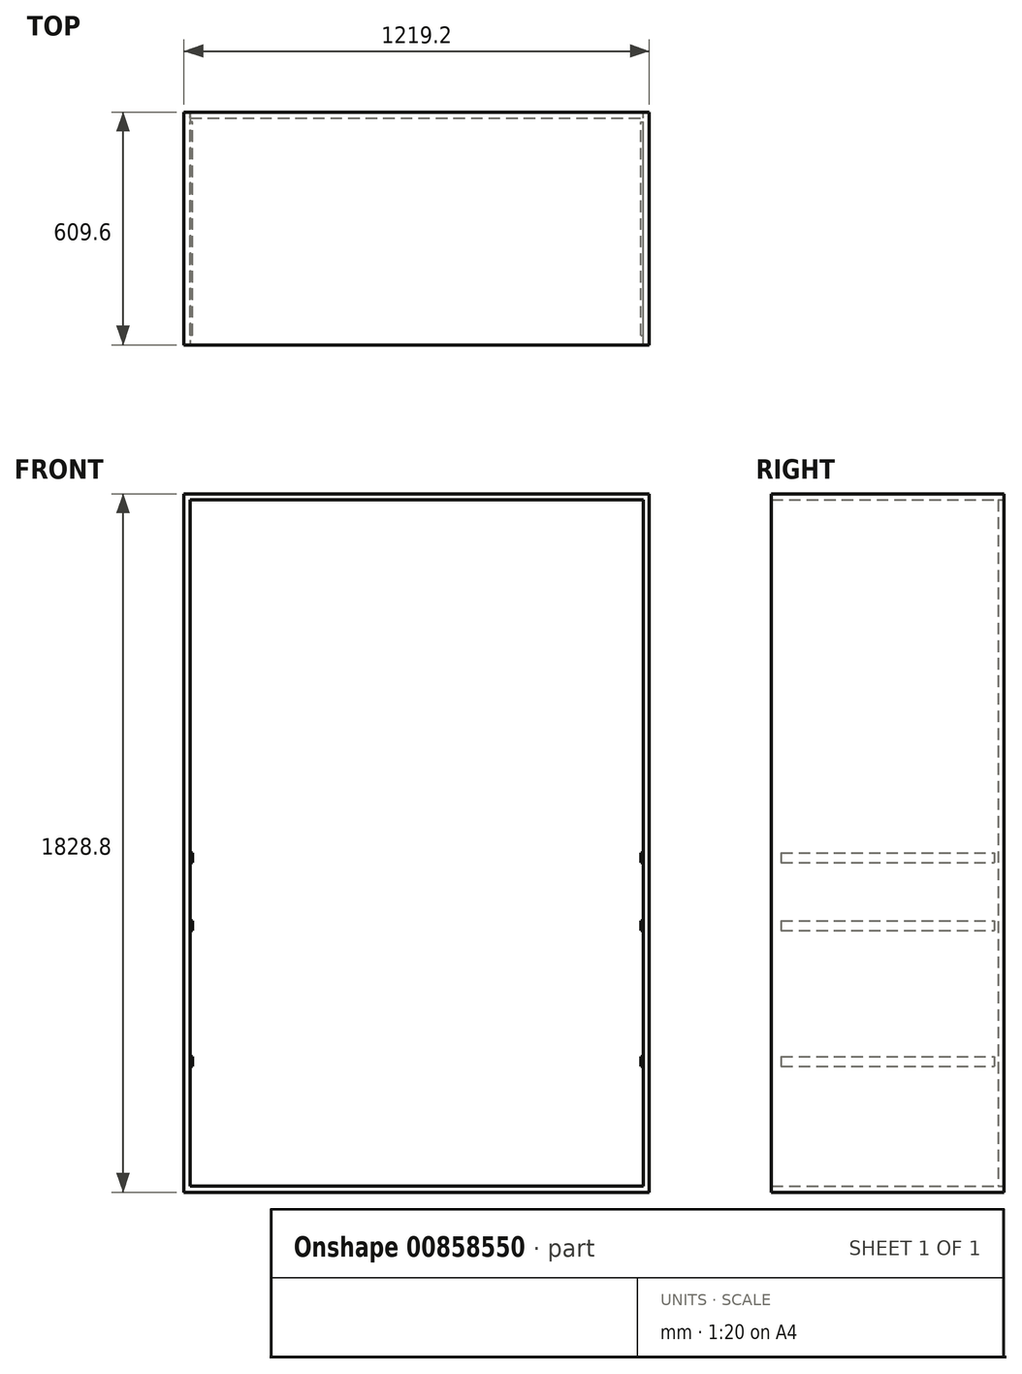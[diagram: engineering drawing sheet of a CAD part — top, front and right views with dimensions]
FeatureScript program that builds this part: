
annotation { "Feature Type Name" : "Feature", "Feature Type Description" : "" }
export const myFeature = defineFeature(function(context is Context, id is Id, definition is map)
    precondition{}
    {
        {
            var Q0;
            Q0=qCreatedBy(makeId("Top.planeOp"),FACE);
            var sketch = newSketch(context, id + "F0", { "sketchPlane" : qUnion([Q0])});
            skLineSegment(sketch, "E0.bottom", {"start": v(-609.6, 304.8) * mm, "end": v(609.6, 304.8) * mm});
            skLineSegment(sketch, "E0.top", {"start": v(-609.6, -304.8) * mm, "end": v(609.6, -304.8) * mm});
            skLineSegment(sketch, "E0.left", {"start": v(-609.6, 304.8) * mm, "end": v(-609.6, -304.8) * mm});
            skLineSegment(sketch, "E0.right", {"start": v(609.6, 304.8) * mm, "end": v(609.6, -304.8) * mm});
            skSolve(sketch);
        }
        {
            var Q0;
            Q0=makeQuery(id+"F0.imprint","IMPRINT",FACE,{"disambiguationData":[TD([[makeQuery(id+"F0.imprint","IMPRINT",EDGE,{"derivedFrom":sQuery(id+"F0.wireOp",EDGE,"E0.bottom")}),-1.0]])]});
            extrude(context, id + "F1", {"entities" : qUnion([Q0]), "depth" : 15.88 * mm, "offsetDistance" : 25.4 * mm});
        }
        {
            var Q0;
            Q0=makeQuery(id+"F1.opExtrude","SWEPT_FACE",FACE,{"disambiguationData":[OSD([sQuery(id+"F0.wireOp",EDGE,"E0.left")])]});
            var sketch = newSketch(context, id + "F2", { "sketchPlane" : qUnion([Q0])});
            skLineSegment(sketch, "E1.bottom", {"start": v(304.8, 0) * mm, "end": v(-304.8, 0) * mm});
            skLineSegment(sketch, "E1.top", {"start": v(304.8, 1828.8) * mm, "end": v(-304.8, 1828.8) * mm});
            skLineSegment(sketch, "E1.left", {"start": v(304.8, 0) * mm, "end": v(304.8, 1828.8) * mm});
            skLineSegment(sketch, "E1.right", {"start": v(-304.8, 0) * mm, "end": v(-304.8, 1828.8) * mm});
            skSolve(sketch);
        }
        {
            var Q0;
            Q0 = qSketchRegion(id + "F2", true);
            extrude(context, id + "F3", {"entities" : qUnion([Q0]), "operationType" : NewBodyOperationType.ADD, "oppositeDirection" : true, "depth" : 15.88 * mm, "offsetDistance" : 25.4 * mm});
        }
        {
            var Q0;
            Q0=makeQuery(id+"F3.opExtrude","SWEPT_FACE",FACE,{"disambiguationData":[OSD([sQuery(id+"F2.wireOp",EDGE,"E1.top")])]});
            var sketch = newSketch(context, id + "F4", { "sketchPlane" : qUnion([Q0])});
            skLineSegment(sketch, "E2.bottom", {"start": v(-609.6, 304.8) * mm, "end": v(609.6, 304.8) * mm});
            skLineSegment(sketch, "E2.top", {"start": v(-609.6, -304.8) * mm, "end": v(609.6, -304.8) * mm});
            skLineSegment(sketch, "E2.left", {"start": v(-609.6, 304.8) * mm, "end": v(-609.6, -304.8) * mm});
            skLineSegment(sketch, "E2.right", {"start": v(609.6, 304.8) * mm, "end": v(609.6, -304.8) * mm});
            skSolve(sketch);
        }
        {
            var Q0;
            {var subQ2=sQuery(id+"F4.wireOp",EDGE,"E2.right");Q0=makeQuery(id+"F4.imprint","IMPRINT",FACE,{"disambiguationData":[TD([[makeQuery(id+"F4.imprint","IMPRINT",EDGE,{"derivedFrom":subQ2}),-1.0]])]});}
            extrude(context, id + "F5", {"entities" : qUnion([Q0]), "operationType" : NewBodyOperationType.ADD, "oppositeDirection" : true, "depth" : 15.88 * mm, "offsetDistance" : 25.4 * mm});
        }
        {
            var Q0;
            Q0=makeQuery(id+"F3.opExtrude","CAP_FACE",FACE,{"disambiguationData":[OSD([sQuery(id+"F2.wireOp",EDGE,"E1.bottom"),sQuery(id+"F2.wireOp",EDGE,"E1.top"),sQuery(id+"F2.wireOp",EDGE,"E1.left"),sQuery(id+"F2.wireOp",EDGE,"E1.right")])],"isStart":false});
            var sketch = newSketch(context, id + "F6", { "sketchPlane" : qUnion([Q0])});
            skLineSegment(sketch, "E3.bottom", {"start": v(-279.4, 355.6) * mm, "end": v(279.4, 355.6) * mm});
            skLineSegment(sketch, "E3.top", {"start": v(-279.4, 330.2) * mm, "end": v(279.4, 330.2) * mm});
            skLineSegment(sketch, "E3.left", {"start": v(-279.4, 355.6) * mm, "end": v(-279.4, 330.2) * mm});
            skLineSegment(sketch, "E3.right", {"start": v(279.4, 355.6) * mm, "end": v(279.4, 330.2) * mm});
            skLineSegment(sketch, "E4.bottom", {"start": v(-279.4, 711.2) * mm, "end": v(279.4, 711.2) * mm});
            skLineSegment(sketch, "E4.top", {"start": v(-279.4, 685.8) * mm, "end": v(279.4, 685.8) * mm});
            skLineSegment(sketch, "E4.left", {"start": v(-279.4, 711.2) * mm, "end": v(-279.4, 685.8) * mm});
            skLineSegment(sketch, "E4.right", {"start": v(279.4, 711.2) * mm, "end": v(279.4, 685.8) * mm});
            skLineSegment(sketch, "E5.bottom", {"start": v(-279.4, 889) * mm, "end": v(279.4, 889) * mm});
            skLineSegment(sketch, "E5.top", {"start": v(-279.4, 863.6) * mm, "end": v(279.4, 863.6) * mm});
            skLineSegment(sketch, "E5.left", {"start": v(-279.4, 889) * mm, "end": v(-279.4, 863.6) * mm});
            skLineSegment(sketch, "E5.right", {"start": v(279.4, 889) * mm, "end": v(279.4, 863.6) * mm});
            skSolve(sketch);
        }
        {
            var Q0;
            Q0 = qSketchRegion(id + "F6", true);
            extrude(context, id + "F7", {"entities" : qUnion([Q0]), "operationType" : NewBodyOperationType.ADD, "depth" : 6.35 * mm, "offsetDistance" : 25.4 * mm});
        }
        {
            var Q0;
            Q0=makeQuery(id+"F1.opExtrude","SWEPT_FACE",FACE,{"disambiguationData":[OSD([sQuery(id+"F0.wireOp",EDGE,"E0.right")])]});
            var sketch = newSketch(context, id + "F8", { "sketchPlane" : qUnion([Q0])});
            skLineSegment(sketch, "E6.bottom", {"start": v(-304.8, 0) * mm, "end": v(304.8, 0) * mm});
            skLineSegment(sketch, "E6.top", {"start": v(-304.8, 1828.8) * mm, "end": v(304.8, 1828.8) * mm});
            skLineSegment(sketch, "E6.left", {"start": v(-304.8, 0) * mm, "end": v(-304.8, 1828.8) * mm});
            skLineSegment(sketch, "E6.right", {"start": v(304.8, 0) * mm, "end": v(304.8, 1828.8) * mm});
            skSolve(sketch);
        }
        {
            var Q0;
            Q0 = qSketchRegion(id + "F8", true);
            extrude(context, id + "F9", {"entities" : qUnion([Q0]), "operationType" : NewBodyOperationType.ADD, "oppositeDirection" : true, "depth" : 15.88 * mm, "offsetDistance" : 25.4 * mm});
        }
        {
            var Q0;
            Q0=makeQuery(id+"F9.boolean.opBoolean","MERGE",FACE,{"derivedFrom":[makeQuery(id+"F5.boolean.opBoolean","MERGE",FACE,{"derivedFrom":[makeQuery(id+"F3.boolean.opBoolean","MERGE",FACE,{"derivedFrom":[makeQuery(id+"F1.opExtrude","SWEPT_FACE",FACE,{"disambiguationData":[OSD([sQuery(id+"F0.wireOp",EDGE,"E0.bottom")])]}),makeQuery(id+"F3.opExtrude","SWEPT_FACE",FACE,{"disambiguationData":[OSD([sQuery(id+"F2.wireOp",EDGE,"E1.right")])]})]}),makeQuery(id+"F5.opExtrude","SWEPT_FACE",FACE,{"disambiguationData":[OSD([sQuery(id+"F4.wireOp",EDGE,"E2.bottom")])]})]}),makeQuery(id+"F9.opExtrude","SWEPT_FACE",FACE,{"disambiguationData":[OSD([sQuery(id+"F8.wireOp",EDGE,"E6.right")])]})]});
            var sketch = newSketch(context, id + "F10", { "sketchPlane" : qUnion([Q0])});
            skLineSegment(sketch, "E7.bottom", {"start": v(-609.6, 0) * mm, "end": v(609.6, 0) * mm});
            skLineSegment(sketch, "E7.top", {"start": v(-609.6, 1828.8) * mm, "end": v(609.6, 1828.8) * mm});
            skLineSegment(sketch, "E7.left", {"start": v(-609.6, 0) * mm, "end": v(-609.6, 1828.8) * mm});
            skLineSegment(sketch, "E7.right", {"start": v(609.6, 0) * mm, "end": v(609.6, 1828.8) * mm});
            skSolve(sketch);
        }
        {
            var Q0;
            Q0=makeQuery(id+"F10.imprint","IMPRINT",FACE,{"disambiguationData":[TD([[makeQuery(id+"F10.imprint","IMPRINT",EDGE,{"derivedFrom":makeQuery(id+"F3.opExtrude","CAP_EDGE",EDGE,{"disambiguationData":[OSD([sQuery(id+"F2.wireOp",EDGE,"E1.right")])],"isStart":false})}),-1.0]])]});
            extrude(context, id + "F11", {"entities" : qUnion([Q0]), "oppositeDirection" : true, "depth" : 15.88 * mm, "offsetDistance" : 25.4 * mm});
        }
        {
            var Q0;
            Q0=makeQuery(id+"F9.opExtrude","CAP_FACE",FACE,{"disambiguationData":[OSD([sQuery(id+"F8.wireOp",EDGE,"E6.bottom"),sQuery(id+"F8.wireOp",EDGE,"E6.top"),sQuery(id+"F8.wireOp",EDGE,"E6.left"),sQuery(id+"F8.wireOp",EDGE,"E6.right")])],"isStart":false});
            var sketch = newSketch(context, id + "F12", { "sketchPlane" : qUnion([Q0])});
            skLineSegment(sketch, "E8.bottom", {"start": v(279.4, 330.2) * mm, "end": v(-279.4, 330.2) * mm});
            skLineSegment(sketch, "E8.top", {"start": v(279.4, 355.6) * mm, "end": v(-279.4, 355.6) * mm});
            skLineSegment(sketch, "E8.left", {"start": v(279.4, 330.2) * mm, "end": v(279.4, 355.6) * mm});
            skLineSegment(sketch, "E8.right", {"start": v(-279.4, 330.2) * mm, "end": v(-279.4, 355.6) * mm});
            skLineSegment(sketch, "E9.bottom", {"start": v(279.4, 685.8) * mm, "end": v(-279.4, 685.8) * mm});
            skLineSegment(sketch, "E9.top", {"start": v(279.4, 711.2) * mm, "end": v(-279.4, 711.2) * mm});
            skLineSegment(sketch, "E9.left", {"start": v(279.4, 685.8) * mm, "end": v(279.4, 711.2) * mm});
            skLineSegment(sketch, "E9.right", {"start": v(-279.4, 685.8) * mm, "end": v(-279.4, 711.2) * mm});
            skLineSegment(sketch, "E10.bottom", {"start": v(279.4, 863.6) * mm, "end": v(-279.4, 863.6) * mm});
            skLineSegment(sketch, "E10.top", {"start": v(279.4, 889) * mm, "end": v(-279.4, 889) * mm});
            skLineSegment(sketch, "E10.left", {"start": v(279.4, 863.6) * mm, "end": v(279.4, 889) * mm});
            skLineSegment(sketch, "E10.right", {"start": v(-279.4, 863.6) * mm, "end": v(-279.4, 889) * mm});
            skSolve(sketch);
        }
        {
            var Q0;
            Q0=makeQuery(id+"F12.imprint","IMPRINT",FACE,{"disambiguationData":[TD([[makeQuery(id+"F12.imprint","IMPRINT",EDGE,{"derivedFrom":sQuery(id+"F12.wireOp",EDGE,"E10.bottom")}),-1.0]])]});
            var Q1;
            Q1=makeQuery(id+"F12.imprint","IMPRINT",FACE,{"disambiguationData":[TD([[makeQuery(id+"F12.imprint","IMPRINT",EDGE,{"derivedFrom":sQuery(id+"F12.wireOp",EDGE,"E8.bottom")}),-1.0]])]});
            var Q2;
            Q2=makeQuery(id+"F12.imprint","IMPRINT",FACE,{"disambiguationData":[TD([[makeQuery(id+"F12.imprint","IMPRINT",EDGE,{"derivedFrom":sQuery(id+"F12.wireOp",EDGE,"E9.bottom")}),-1.0]])]});
            extrude(context, id + "F13", {"entities" : qUnion([Q0, Q1, Q2]), "operationType" : NewBodyOperationType.ADD, "depth" : 6.35 * mm, "offsetDistance" : 25.4 * mm});
        }
    });
